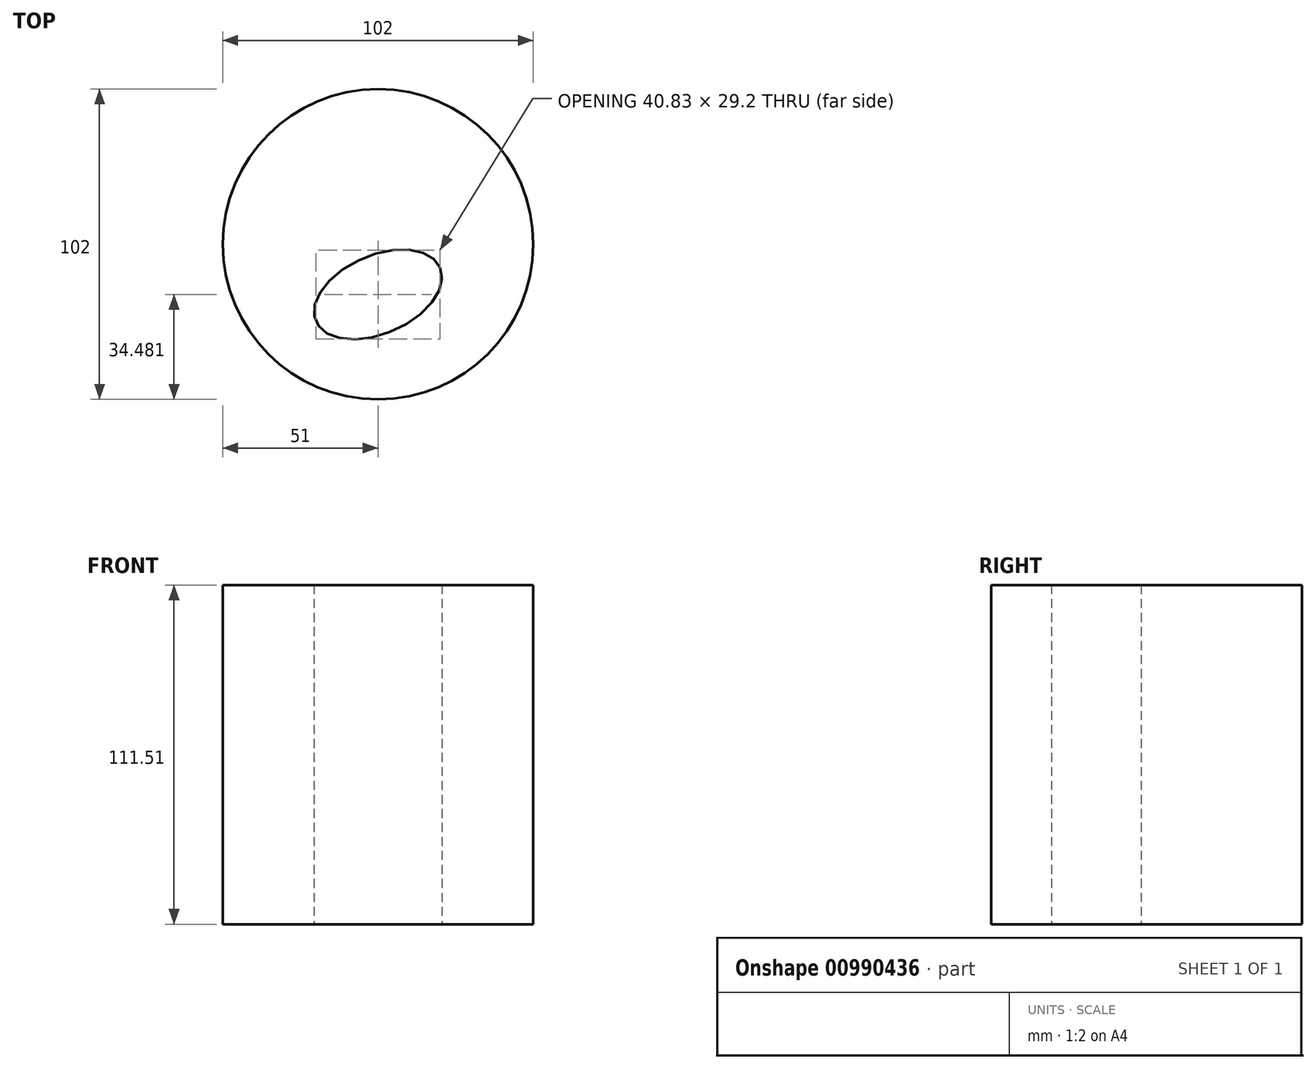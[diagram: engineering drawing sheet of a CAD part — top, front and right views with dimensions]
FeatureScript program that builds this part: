
annotation { "Feature Type Name" : "Feature", "Feature Type Description" : "" }
export const myFeature = defineFeature(function(context is Context, id is Id, definition is map)
    precondition{}
    {
        {
            var Q0;
            Q0=qCreatedBy(makeId("Top.planeOp"),FACE);
            var sketch = newSketch(context, id + "F0", { "sketchPlane" : qUnion([Q0])});
            skCircle(sketch, "E0", {"center": v(0, 0) * mm, "radius": 51 * mm});
            skSolve(sketch);
        }
        {
            var Q0;
            Q0=makeQuery(id+"F0.imprint","IMPRINT",FACE,{"disambiguationData":[TD([[makeQuery(id+"F0.imprint","IMPRINT",EDGE,{"derivedFrom":sQuery(id+"F0.wireOp",EDGE,"E0")}),1.0]])]});
            extrude(context, id + "F1", {"entities" : qUnion([Q0]), "depth" : 111.5 * mm, "offsetDistance" : 25.4 * mm});
        }
        {
            var Q0;
            Q0=makeQuery(id+"F1.opExtrude","CAP_FACE",FACE,{"disambiguationData":[OSD([sQuery(id+"F0.wireOp",EDGE,"E0")])],"isStart":false});
            var sketch = newSketch(context, id + "F2", { "sketchPlane" : qUnion([Q0])});
            skEllipse(sketch, "E1", {"center": v(0, -16.52) * mm, "majorRadius": 22.24 * mm, "minorRadius": 12.89 * mm, "majorAxis": v(0.92, 0.4)});
            skSolve(sketch);
        }
        {
            var Q0;
            Q0=makeQuery(id+"F2.imprint","IMPRINT",FACE,{"disambiguationData":[TD([[makeQuery(id+"F2.imprint","IMPRINT",EDGE,{"derivedFrom":sQuery(id+"F2.wireOp",EDGE,"E1")}),1.0]])]});
            extrude(context, id + "F3", {"entities" : qUnion([Q0]), "operationType" : NewBodyOperationType.ADD, "depth" : 25.4 * mm, "offsetDistance" : 25.4 * mm});
        }
        {
            var Q0;
            Q0=makeQuery(id+"F3.opExtrude","CAP_FACE",FACE,{"disambiguationData":[OSD([sQuery(id+"F2.wireOp",EDGE,"E1")])],"isStart":false});
            extrude(context, id + "F4", {"entities" : qUnion([Q0]), "operationType" : NewBodyOperationType.REMOVE, "oppositeDirection" : true, "depth" : 219.96 * mm, "offsetDistance" : 25.4 * mm});
        }
    });
